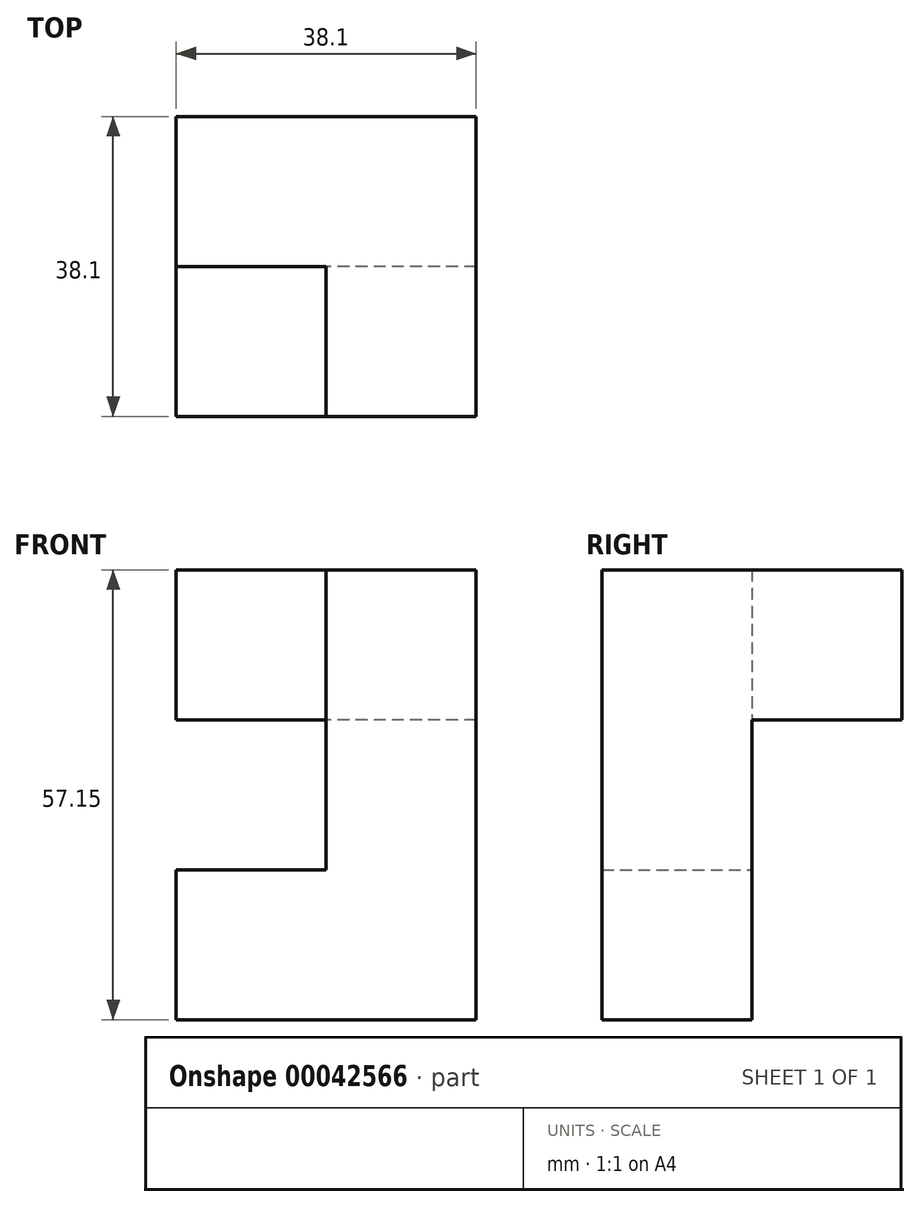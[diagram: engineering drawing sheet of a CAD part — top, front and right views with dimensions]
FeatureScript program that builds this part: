
annotation { "Feature Type Name" : "Feature", "Feature Type Description" : "" }
export const myFeature = defineFeature(function(context is Context, id is Id, definition is map)
    precondition{}
    {
        {
            var Q0;
            Q0=qCreatedBy(makeId("Top.planeOp"),FACE);
            var sketch = newSketch(context, id + "F0", { "sketchPlane" : qUnion([Q0])});
            skLineSegment(sketch, "E0.bottom", {"start": v(0, 0) * mm, "end": v(-19.05, 0) * mm});
            skLineSegment(sketch, "E0.top", {"start": v(0, 19.05) * mm, "end": v(-19.05, 19.05) * mm});
            skLineSegment(sketch, "E0.left", {"start": v(0, 0) * mm, "end": v(0, 19.05) * mm});
            skLineSegment(sketch, "E0.right", {"start": v(-19.05, 0) * mm, "end": v(-19.05, 19.05) * mm});
            skSolve(sketch);
        }
        {
            var Q0;
            Q0=makeQuery(id+"F0.imprint","IMPRINT",FACE,{"disambiguationData":[TD([[makeQuery(id+"F0.imprint","IMPRINT",EDGE,{"derivedFrom":sQuery(id+"F0.wireOp",EDGE,"E0.bottom")}),-1.0]])]});
            extrude(context, id + "F1", {"entities" : qUnion([Q0]), "depth" : 57.15 * mm});
        }
        {
            var Q0;
            Q0=makeQuery(id+"F1.opExtrude","SWEPT_FACE",FACE,{"disambiguationData":[OSD([sQuery(id+"F0.wireOp",EDGE,"E0.top")])]});
            var sketch = newSketch(context, id + "F2", { "sketchPlane" : qUnion([Q0])});
            skLineSegment(sketch, "E1.bottom", {"start": v(0, 57.15) * mm, "end": v(19.05, 57.15) * mm});
            skLineSegment(sketch, "E1.top", {"start": v(0, 38.1) * mm, "end": v(19.05, 38.1) * mm});
            skLineSegment(sketch, "E1.left", {"start": v(0, 57.15) * mm, "end": v(0, 38.1) * mm});
            skLineSegment(sketch, "E1.right", {"start": v(19.05, 57.15) * mm, "end": v(19.05, 38.1) * mm});
            skSolve(sketch);
        }
        {
            var Q0;
            Q0=makeQuery(id+"F2.imprint","IMPRINT",FACE,{"disambiguationData":[TD([[makeQuery(id+"F2.imprint","IMPRINT",EDGE,{"derivedFrom":sQuery(id+"F2.wireOp",EDGE,"E1.bottom")}),-1.0]])]});
            extrude(context, id + "F3", {"entities" : qUnion([Q0]), "operationType" : NewBodyOperationType.ADD, "depth" : 19.05 * mm});
        }
        {
            var Q0;
            Q0=makeQuery(id+"F3.boolean.opBoolean","MERGE",FACE,{"derivedFrom":[makeQuery(id+"F1.opExtrude","SWEPT_FACE",FACE,{"disambiguationData":[OSD([sQuery(id+"F0.wireOp",EDGE,"E0.right")])]}),makeQuery(id+"F3.opExtrude","SWEPT_FACE",FACE,{"disambiguationData":[OSD([sQuery(id+"F2.wireOp",EDGE,"E1.right")])]})]});
            var sketch = newSketch(context, id + "F4", { "sketchPlane" : qUnion([Q0])});
            skLineSegment(sketch, "E2.bottom", {"start": v(-38.1, 57.15) * mm, "end": v(-19.05, 57.15) * mm});
            skLineSegment(sketch, "E2.top", {"start": v(-38.1, 38.1) * mm, "end": v(-19.05, 38.1) * mm});
            skLineSegment(sketch, "E2.left", {"start": v(-38.1, 57.15) * mm, "end": v(-38.1, 38.1) * mm});
            skLineSegment(sketch, "E2.right", {"start": v(-19.05, 57.15) * mm, "end": v(-19.05, 38.1) * mm});
            skSolve(sketch);
        }
        {
            var Q0;
            Q0=makeQuery(id+"F4.imprint","IMPRINT",FACE,{"disambiguationData":[TD([[makeQuery(id+"F4.imprint","IMPRINT",EDGE,{"derivedFrom":sQuery(id+"F4.wireOp",EDGE,"E2.bottom")}),1.0]])]});
            extrude(context, id + "F5", {"entities" : qUnion([Q0]), "operationType" : NewBodyOperationType.ADD, "depth" : 19.05 * mm});
        }
        {
            var Q0;
            Q0=makeQuery(id+"F3.boolean.opBoolean","MERGE",FACE,{"derivedFrom":[makeQuery(id+"F1.opExtrude","SWEPT_FACE",FACE,{"disambiguationData":[OSD([sQuery(id+"F0.wireOp",EDGE,"E0.right")])]}),makeQuery(id+"F3.opExtrude","SWEPT_FACE",FACE,{"disambiguationData":[OSD([sQuery(id+"F2.wireOp",EDGE,"E1.right")])]})]});
            var sketch = newSketch(context, id + "F6", { "sketchPlane" : qUnion([Q0])});
            skLineSegment(sketch, "E3.bottom", {"start": v(0, 0) * mm, "end": v(-19.05, 0) * mm});
            skLineSegment(sketch, "E3.top", {"start": v(0, 19.05) * mm, "end": v(-19.05, 19.05) * mm});
            skLineSegment(sketch, "E3.left", {"start": v(0, 0) * mm, "end": v(0, 19.05) * mm});
            skLineSegment(sketch, "E3.right", {"start": v(-19.05, 0) * mm, "end": v(-19.05, 19.05) * mm});
            skSolve(sketch);
        }
        {
            var Q0;
            Q0=makeQuery(id+"F6.imprint","IMPRINT",FACE,{"disambiguationData":[TD([[makeQuery(id+"F6.imprint","IMPRINT",EDGE,{"derivedFrom":sQuery(id+"F6.wireOp",EDGE,"E3.bottom")}),-1.0]])]});
            extrude(context, id + "F7", {"entities" : qUnion([Q0]), "operationType" : NewBodyOperationType.ADD, "depth" : 19.05 * mm});
        }
    });
